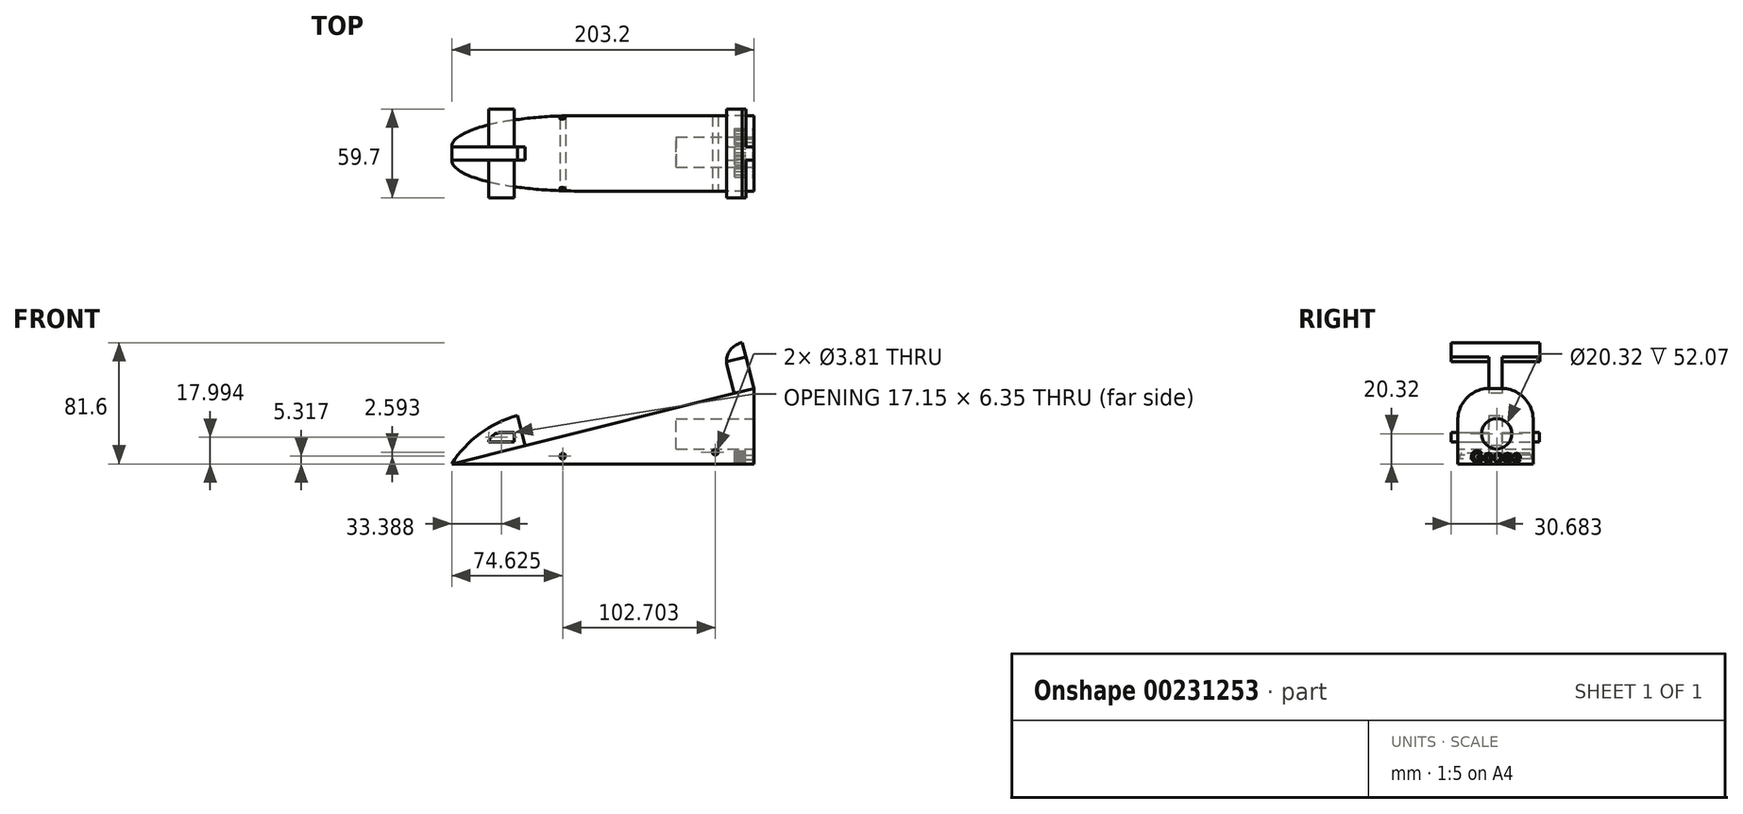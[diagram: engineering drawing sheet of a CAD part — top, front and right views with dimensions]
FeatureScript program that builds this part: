
annotation { "Feature Type Name" : "Feature", "Feature Type Description" : "" }
export const myFeature = defineFeature(function(context is Context, id is Id, definition is map)
    precondition{}
    {
        {
            var Q0;
            Q0=qCreatedBy(makeId("Front.planeOp"),FACE);
            var sketch = newSketch(context, id + "F0", { "sketchPlane" : qUnion([Q0])});
            skLineSegment(sketch, "E0", {"start": v(-101.26, 0) * mm, "end": v(101.94, 0) * mm});
            skLineSegment(sketch, "E1", {"start": v(101.94, 0) * mm, "end": v(101.94, 50.8) * mm});
            skLineSegment(sketch, "E2", {"start": v(101.94, 50.8) * mm, "end": v(-101.26, 0) * mm});
            skSolve(sketch);
        }
        {
            var Q0;
            Q0=makeQuery(id+"F0.imprint","IMPRINT",FACE,{"disambiguationData":[TD([[makeQuery(id+"F0.imprint","IMPRINT",EDGE,{"derivedFrom":sQuery(id+"F0.wireOp",EDGE,"E0")}),1.0]])]});
            extrude(context, id + "F1", {"entities" : qUnion([Q0]), "depth" : 50.8 * mm});
        }
        {
            var Q0;
            Q0=makeQuery(id+"F1.opExtrude","SWEPT_FACE",FACE,{"disambiguationData":[OSD([sQuery(id+"F0.wireOp",EDGE,"E1")])]});
            var sketch = newSketch(context, id + "F2", { "sketchPlane" : qUnion([Q0])});
            skCircle(sketch, "E3", {"center": v(-24.57, 20.32) * mm, "radius": 10.16 * mm});
            skSolve(sketch);
        }
        {
            var Q0;
            Q0=makeQuery(id+"F2.imprint","IMPRINT",FACE,{"disambiguationData":[TD([[makeQuery(id+"F2.imprint","IMPRINT",EDGE,{"derivedFrom":sQuery(id+"F2.wireOp",EDGE,"E3")}),1.0]])]});
            var Q1;
            Q1=sQuery(id+"F2.wireOp",EDGE,"E3");
            extrude(context, id + "F3", {"entities" : qUnion([Q0]), "operationType" : NewBodyOperationType.REMOVE, "surfaceEntities" : qUnion([Q1]), "oppositeDirection" : true, "depth" : 52.07 * mm});
        }
        {
            var Q0;
            Q0=makeQuery(id+"F1.opExtrude","CAP_EDGE",EDGE,{"disambiguationData":[OSD([sQuery(id+"F0.wireOp",EDGE,"E2")])],"isStart":false});
            var Q1;
            Q1=makeQuery(id+"F1.opExtrude","CAP_EDGE",EDGE,{"disambiguationData":[OSD([sQuery(id+"F0.wireOp",EDGE,"E2")])],"isStart":true});
            fillet(context, id + "F4", {"entities" : qUnion([Q0, Q1]), "radius" : 20.95 * mm, "tangentPropagation" : true, "allowEdgeOverflow" : false});
        }
        {
            var Q0;
            Q0=makeQuery(id+"F1.opExtrude","SWEPT_FACE",FACE,{"disambiguationData":[OSD([sQuery(id+"F0.wireOp",EDGE,"E2")])]});
            var sketch = newSketch(context, id + "F5", { "sketchPlane" : qUnion([Q0])});
            skLineSegment(sketch, "E4", {"start": v(-98.24, -20.96) * mm, "end": v(-47.44, -20.96) * mm});
            skLineSegment(sketch, "E5", {"start": v(-47.44, -20.95) * mm, "end": v(-47.44, -29.84) * mm});
            skLineSegment(sketch, "E6", {"start": v(-47.44, -29.85) * mm, "end": v(-98.24, -29.85) * mm});
            skLineSegment(sketch, "E7", {"start": v(-98.24, -29.85) * mm, "end": v(-98.24, -20.96) * mm});
            skSolve(sketch);
        }
        {
            var Q0;
            Q0=makeQuery(id+"F5.imprint","IMPRINT",FACE,{"disambiguationData":[TD([[makeQuery(id+"F5.imprint","IMPRINT",EDGE,{"derivedFrom":sQuery(id+"F5.wireOp",EDGE,"E4")}),1.0]])]});
            extrude(context, id + "F6", {"entities" : qUnion([Q0]), "operationType" : NewBodyOperationType.ADD, "depth" : 20.95 * mm});
        }
        {
            var Q0;
            Q0=makeQuery(id+"F6.opExtrude","CAP_EDGE",EDGE,{"disambiguationData":[OSD([sQuery(id+"F5.wireOp",EDGE,"E7")])],"isStart":false});
            fillet(context, id + "F7", {"entities" : qUnion([Q0]), "radius" : 76.2 * mm, "tangentPropagation" : true, "allowEdgeOverflow" : false});
        }
        {
            var Q0;
            Q0=makeQuery(id+"F6.opExtrude","SWEPT_FACE",FACE,{"disambiguationData":[OSD([sQuery(id+"F5.wireOp",EDGE,"E6")])]});
            var sketch = newSketch(context, id + "F8", { "sketchPlane" : qUnion([Q0])});
            skLineSegment(sketch, "E8", {"start": v(-76.44, 21.17) * mm, "end": v(-59.3, 21.17) * mm});
            skLineSegment(sketch, "E9", {"start": v(-59.3, 21.17) * mm, "end": v(-59.3, 14.82) * mm});
            skLineSegment(sketch, "E10", {"start": v(-59.3, 14.82) * mm, "end": v(-76.44, 14.82) * mm});
            skLineSegment(sketch, "E11", {"start": v(-76.44, 14.82) * mm, "end": v(-76.44, 21.17) * mm});
            skSolve(sketch);
        }
        {
            var Q0;
            Q0=makeQuery(id+"F8.imprint","IMPRINT",FACE,{"disambiguationData":[TD([[makeQuery(id+"F8.imprint","IMPRINT",EDGE,{"derivedFrom":sQuery(id+"F8.wireOp",EDGE,"E8")}),-1.0]])]});
            extrude(context, id + "F9", {"entities" : qUnion([Q0]), "operationType" : NewBodyOperationType.ADD, "depth" : 25.4 * mm, "hasSecondDirection" : true, "secondDirectionOppositeDirection" : true, "secondDirectionDepth" : 34.04 * mm});
        }
        {
            var Q0;
            {var subQ0=sQuery(id+"F8.wireOp",EDGE,"E8");var subQ1=sQuery(id+"F8.wireOp",EDGE,"E11");Q0=makeQuery(id+"F9.boolean.opBoolean","SPLIT",EDGE,{"disambiguationData":[TD([makeQuery(id+"F6.opExtrude","SWEPT_FACE",FACE,{"disambiguationData":[OSD([sQuery(id+"F5.wireOp",EDGE,"E6")])]})])],"derivedFrom":makeQuery(id+"F9.opExtrude","SWEPT_EDGE",EDGE,{"disambiguationData":[OSD([subQ0,subQ1])]})});}
            var Q1;
            {var subQ0=sQuery(id+"F8.wireOp",EDGE,"E8");var subQ1=sQuery(id+"F8.wireOp",EDGE,"E11");Q1=makeQuery(id+"F9.boolean.opBoolean","SPLIT",EDGE,{"disambiguationData":[TD([makeQuery(id+"F6.opExtrude","SWEPT_FACE",FACE,{"disambiguationData":[OSD([sQuery(id+"F5.wireOp",EDGE,"E4")])]})])],"derivedFrom":makeQuery(id+"F9.opExtrude","SWEPT_EDGE",EDGE,{"disambiguationData":[OSD([subQ0,subQ1])]})});}
            fillet(context, id + "F10", {"entities" : qUnion([Q0, Q1]), "radius" : 8.9 * mm, "tangentPropagation" : true, "allowEdgeOverflow" : false});
        }
        {
            var Q0;
            Q0=makeQuery(id+"F1.opExtrude","CAP_FACE",FACE,{"disambiguationData":[OSD([sQuery(id+"F0.wireOp",EDGE,"E0"),sQuery(id+"F0.wireOp",EDGE,"E1"),sQuery(id+"F0.wireOp",EDGE,"E2")])],"isStart":false});
            var sketch = newSketch(context, id + "F11", { "sketchPlane" : qUnion([Q0])});
            skCircle(sketch, "E12", {"center": v(76.07, 7.91) * mm, "radius": 2.4 * mm});
            skCircle(sketch, "E13", {"center": v(-26.64, 5.32) * mm, "radius": 1.9 * mm});
            skSolve(sketch);
        }
        {
            var Q0;
            Q0=sQuery(id+"F11.wireOp",VERTEX,"E13.center");
            var Q1;
            Q1=sQuery(id+"F11.wireOp",VERTEX,"E12.center");
            var Q2;
            Q2=makeQuery(id+"F1.opExtrude","SWEPT_BODY",BODY,{"disambiguationData":[OSD([sQuery(id+"F0.wireOp",EDGE,"E0"),sQuery(id+"F0.wireOp",EDGE,"E1"),sQuery(id+"F0.wireOp",EDGE,"E2")])]});
            hole(context, id + "F12", {"style" : HoleStyle.SIMPLE, "endStyle" : HoleEndStyle.THROUGH, "holeDiameter" : 3.8 * mm, "locations" : qUnion([Q0, Q1]), "scope" : qUnion([Q2]), "isTappedThrough" : true});
        }
        {
            var Q0;
            Q0=makeQuery(id+"F1.opExtrude","SWEPT_FACE",FACE,{"disambiguationData":[OSD([sQuery(id+"F0.wireOp",EDGE,"E1")])]});
            var sketch = newSketch(context, id + "F13", { "sketchPlane" : qUnion([Q0])});
            skText(sketch, "E14", { "text": "Goose", "fontName": "Arimo-Bold.ttf"});
            const initialGuessF13  = {"E14": [-0.04197, 0.00125, 1, 0, 0.0078]};
            skSetInitialGuess(sketch, initialGuessF13);
            skSolve(sketch);
        }
        {
            var Q0;
            Q0 = qSketchRegion(id + "F13", true);
            extrude(context, id + "F14", {"entities" : qUnion([Q0]), "operationType" : NewBodyOperationType.REMOVE, "oppositeDirection" : true, "depth" : 12.7 * mm});
        }
        {
            var Q0;
            Q0=makeQuery(id+"F1.opExtrude","SWEPT_FACE",FACE,{"disambiguationData":[OSD([sQuery(id+"F0.wireOp",EDGE,"E2")])]});
            var sketch = newSketch(context, id + "F15", { "sketchPlane" : qUnion([Q0])});
            skLineSegment(sketch, "E15", {"start": v(111.21, -20.96) * mm, "end": v(97.55, -20.96) * mm});
            skLineSegment(sketch, "E16", {"start": v(97.55, -20.96) * mm, "end": v(97.55, -29.85) * mm});
            skLineSegment(sketch, "E17", {"start": v(97.55, -29.85) * mm, "end": v(111.21, -29.85) * mm});
            skLineSegment(sketch, "E18", {"start": v(111.21, -29.85) * mm, "end": v(111.21, -20.96) * mm});
            skSolve(sketch);
        }
        {
            var Q0;
            Q0=makeQuery(id+"F15.imprint","IMPRINT",FACE,{"disambiguationData":[TD([[makeQuery(id+"F15.imprint","IMPRINT",EDGE,{"derivedFrom":sQuery(id+"F15.wireOp",EDGE,"E15")}),1.0]])]});
            extrude(context, id + "F16", {"entities" : qUnion([Q0]), "operationType" : NewBodyOperationType.ADD, "depth" : 31.75 * mm});
        }
        {
            var Q0;
            Q0=makeQuery(id+"F16.opExtrude","SWEPT_FACE",FACE,{"disambiguationData":[OSD([sQuery(id+"F15.wireOp",EDGE,"E15")])]});
            var sketch = newSketch(context, id + "F17", { "sketchPlane" : qUnion([Q0])});
            skLineSegment(sketch, "E19", {"start": v(-94.24, 81.6) * mm, "end": v(-96.6, 72.12) * mm});
            skLineSegment(sketch, "E20", {"start": v(-96.6, 72.12) * mm, "end": v(-83.35, 68.8) * mm});
            skLineSegment(sketch, "E21", {"start": v(-83.35, 68.8) * mm, "end": v(-80.98, 78.29) * mm});
            skLineSegment(sketch, "E22", {"start": v(-80.98, 78.29) * mm, "end": v(-94.24, 81.6) * mm});
            skSolve(sketch);
        }
        {
            var Q0;
            Q0=makeQuery(id+"F17.imprint","IMPRINT",FACE,{"disambiguationData":[TD([[makeQuery(id+"F17.imprint","IMPRINT",EDGE,{"derivedFrom":sQuery(id+"F17.wireOp",EDGE,"E19")}),1.0]])]});
            extrude(context, id + "F18", {"entities" : qUnion([Q0]), "operationType" : NewBodyOperationType.ADD, "depth" : 25.4 * mm});
        }
        {
            var Q0;
            Q0=makeQuery(id+"F16.opExtrude","SWEPT_FACE",FACE,{"disambiguationData":[OSD([sQuery(id+"F15.wireOp",EDGE,"E17")])]});
            var sketch = newSketch(context, id + "F19", { "sketchPlane" : qUnion([Q0])});
            skLineSegment(sketch, "E23", {"start": v(80.98, 78.29) * mm, "end": v(83.35, 68.8) * mm});
            skLineSegment(sketch, "E24", {"start": v(83.35, 68.8) * mm, "end": v(96.6, 72.12) * mm});
            skLineSegment(sketch, "E25", {"start": v(96.6, 72.12) * mm, "end": v(94.24, 81.6) * mm});
            skLineSegment(sketch, "E26", {"start": v(94.24, 81.6) * mm, "end": v(80.98, 78.29) * mm});
            skSolve(sketch);
        }
        {
            var Q0;
            Q0=makeQuery(id+"F19.imprint","IMPRINT",FACE,{"disambiguationData":[TD([[makeQuery(id+"F19.imprint","IMPRINT",EDGE,{"derivedFrom":sQuery(id+"F19.wireOp",EDGE,"E23")}),1.0]])]});
            extrude(context, id + "F20", {"entities" : qUnion([Q0]), "operationType" : NewBodyOperationType.ADD, "depth" : 25.4 * mm});
        }
        {
            var Q0;
            Q0=makeQuery(id+"F20.boolean.opBoolean","MERGE",EDGE,{"derivedFrom":[makeQuery(id+"F18.boolean.opBoolean","MERGE",EDGE,{"derivedFrom":[makeQuery(id+"F16.opExtrude","CAP_EDGE",EDGE,{"disambiguationData":[OSD([sQuery(id+"F15.wireOp",EDGE,"E16")])],"isStart":false}),makeQuery(id+"F18.opExtrude","SWEPT_EDGE",EDGE,{"disambiguationData":[OSD([sQuery(id+"F17.wireOp",EDGE,"E21"),sQuery(id+"F17.wireOp",EDGE,"E22")])]})]}),makeQuery(id+"F20.opExtrude","SWEPT_EDGE",EDGE,{"disambiguationData":[OSD([sQuery(id+"F19.wireOp",EDGE,"E23"),sQuery(id+"F19.wireOp",EDGE,"E26")])]})]});
            fillet(context, id + "F21", {"entities" : qUnion([Q0]), "radius" : 12.7 * mm, "tangentPropagation" : true, "allowEdgeOverflow" : false});
        }
    });
